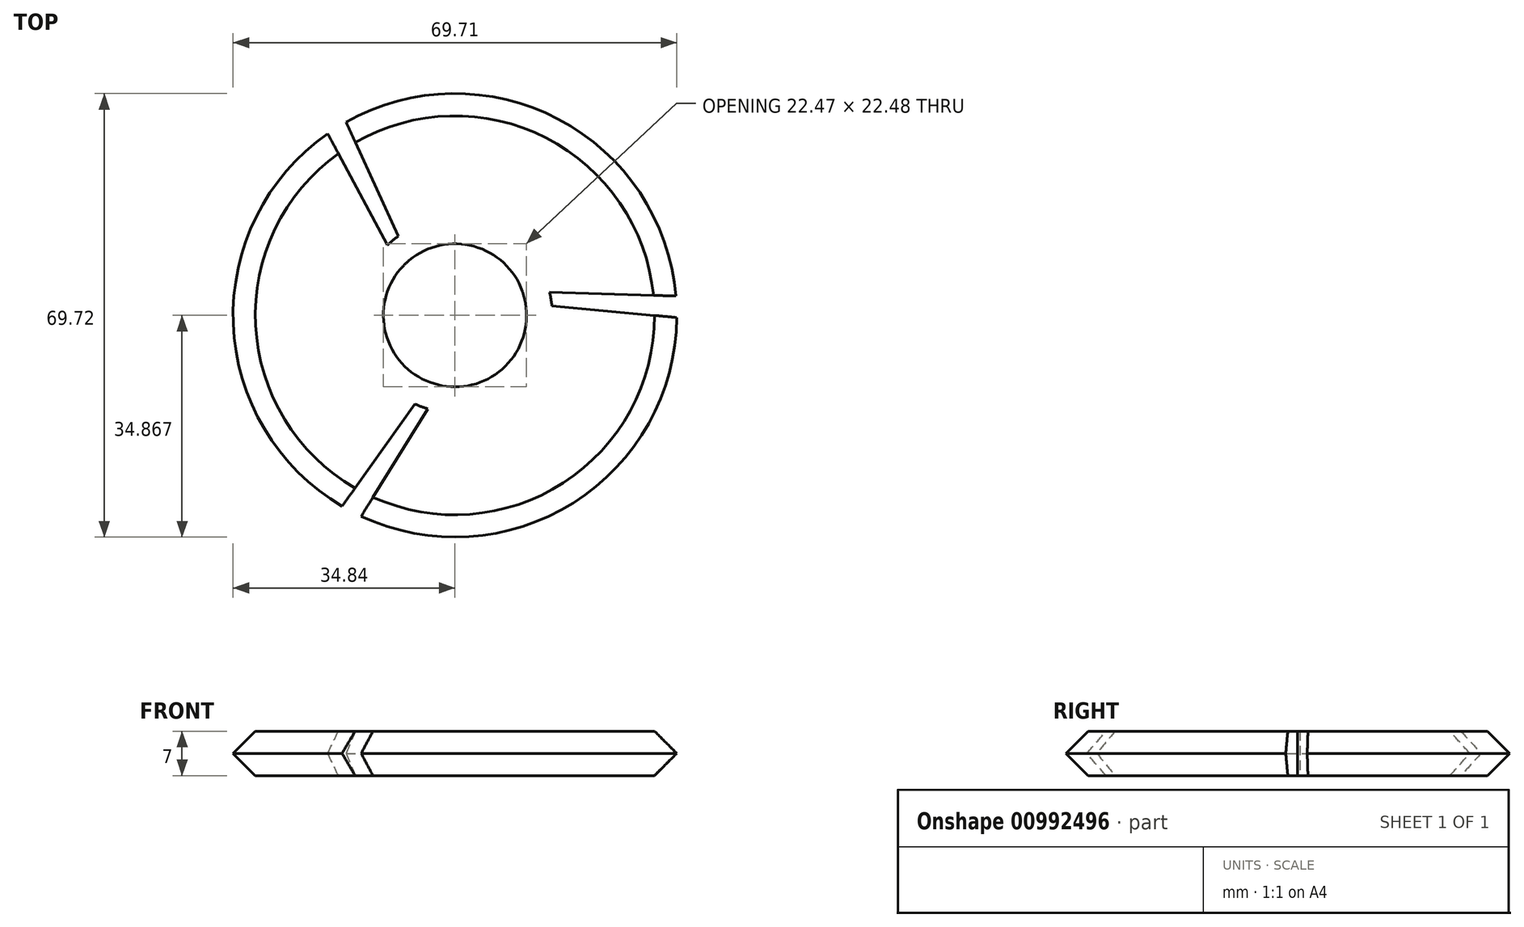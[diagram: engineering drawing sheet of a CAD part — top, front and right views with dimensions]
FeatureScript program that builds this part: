
annotation { "Feature Type Name" : "Feature", "Feature Type Description" : "" }
export const myFeature = defineFeature(function(context is Context, id is Id, definition is map)
    precondition{}
    {
        {
            var Q0;
            Q0=qCreatedBy(makeId("Top.planeOp"),FACE);
            var sketch = newSketch(context, id + "F0", { "sketchPlane" : qUnion([Q0])});
            skArc(sketch, "E0", {"start": v(-12.4, -17.28) * mm, "mid": v(-2.48, -14.21) * mm, "end": v(0.7, -4.33) * mm});
            skCircle(sketch, "E1", {"center": v(-10.39, -6.21) * mm, "radius": 35.36 * mm});
            skLineSegment(sketch, "E2", {"start": v(-14.3, -16.76) * mm, "end": v(-28.4, -36.63) * mm});
            skLineSegment(sketch, "E3", {"start": v(-28.4, -36.63) * mm, "end": v(-25.39, -38.23) * mm});
            skLineSegment(sketch, "E4", {"start": v(-25.39, -38.23) * mm, "end": v(-12.4, -17.28) * mm});
            skLineSegment(sketch, "E5", {"start": v(-12.4, -17.28) * mm, "end": v(-14.3, -16.76) * mm});
            skLineSegment(sketch, "E6.1.0", {"start": v(24.84, -3.2) * mm, "end": v(0.2, -2.42) * mm});
            skLineSegment(sketch, "E6.1.1", {"start": v(0.7, -4.33) * mm, "end": v(24.97, -6.6) * mm});
            skLineSegment(sketch, "E6.2.0", {"start": v(-30.61, 22.8) * mm, "end": v(-18.96, 1.07) * mm});
            skLineSegment(sketch, "E6.2.1", {"start": v(-17.56, 2.45) * mm, "end": v(-27.72, 24.6) * mm});
            skCircle(sketch, "E7", {"center": v(-10.39, -6.21) * mm, "radius": 15.3 * mm});
            skCircle(sketch, "E8", {"center": v(-10.39, -6.21) * mm, "radius": 40.8 * mm});
            skArc(sketch, "E9.trimOffspring", {"start": v(-18.96, 1.07) * mm, "mid": v(-21.27, -9.06) * mm, "end": v(-14.3, -16.76) * mm});
            skArc(sketch, "E10.trimOffspring", {"start": v(0.2, -2.42) * mm, "mid": v(-7.4, 4.64) * mm, "end": v(-17.56, 2.45) * mm});
            skArc(sketch, "E11", {"start": v(0.7, -4.33) * mm, "mid": v(0.48, -3.37) * mm, "end": v(0.2, -2.42) * mm});
            skArc(sketch, "E12", {"start": v(-17.56, 2.45) * mm, "mid": v(-18.28, 1.78) * mm, "end": v(-18.96, 1.07) * mm});
            skSolve(sketch);
        }
        {
            var Q0;
            {var subQ1=sQuery(id+"F0.wireOp",EDGE,"E1");var subQ3=sQuery(id+"F0.wireOp",EDGE,"E6.2.0");var subQ4=makeQuery(id+"F0.imprint","INTERSECT",VERTEX,{"derivedFrom":[subQ1,subQ3]});Q0=makeQuery(id+"F0.imprint","IMPRINT",FACE,{"disambiguationData":[TD([[makeQuery(id+"F0.imprint","IMPRINT",EDGE,{"disambiguationData":[TD([[subQ4,-1.0]])],"derivedFrom":subQ3}),-1.0]])]});}
            var Q1;
            {var subQ0=sQuery(id+"F0.wireOp",EDGE,"E6.1.0");var subQ1=sQuery(id+"F0.wireOp",EDGE,"E1");var subQ2=makeQuery(id+"F0.imprint","INTERSECT",VERTEX,{"derivedFrom":[subQ1,subQ0]});Q1=makeQuery(id+"F0.imprint","IMPRINT",FACE,{"disambiguationData":[TD([[makeQuery(id+"F0.imprint","IMPRINT",EDGE,{"disambiguationData":[TD([[subQ2,-1.0]])],"derivedFrom":subQ1}),1.0]])]});}
            var Q2;
            {var subQ1=sQuery(id+"F0.wireOp",EDGE,"E1");var subQ3=sQuery(id+"F0.wireOp",EDGE,"E6.1.1");var subQ4=makeQuery(id+"F0.imprint","INTERSECT",VERTEX,{"derivedFrom":[subQ1,subQ3]});Q2=makeQuery(id+"F0.imprint","IMPRINT",FACE,{"disambiguationData":[TD([[makeQuery(id+"F0.imprint","IMPRINT",EDGE,{"disambiguationData":[TD([[subQ4,1.0]])],"derivedFrom":subQ3}),-1.0]])]});}
            var Q3;
            {var subQ0=sQuery(id+"F0.wireOp",EDGE,"E9.trimOffspring");Q3=makeQuery(id+"F0.imprint","IMPRINT",FACE,{"disambiguationData":[TD([[makeQuery(id+"F0.imprint","IMPRINT",EDGE,{"derivedFrom":subQ0}),-1.0]])]});}
            var Q4;
            {var subQ0=sQuery(id+"F0.wireOp",EDGE,"E10.trimOffspring");Q4=makeQuery(id+"F0.imprint","IMPRINT",FACE,{"disambiguationData":[TD([[makeQuery(id+"F0.imprint","IMPRINT",EDGE,{"derivedFrom":subQ0}),-1.0]])]});}
            var Q5;
            {var subQ0=sQuery(id+"F0.wireOp",EDGE,"E0");Q5=makeQuery(id+"F0.imprint","IMPRINT",FACE,{"disambiguationData":[TD([[makeQuery(id+"F0.imprint","IMPRINT",EDGE,{"derivedFrom":subQ0}),-1.0]])]});}
            var Q6;
            {var subQ0=sQuery(id+"F0.wireOp",EDGE,"E12");Q6=makeQuery(id+"F0.imprint","IMPRINT",FACE,{"disambiguationData":[TD([[makeQuery(id+"F0.imprint","IMPRINT",EDGE,{"derivedFrom":subQ0}),-1.0]])]});}
            var Q7;
            {var subQ0=sQuery(id+"F0.wireOp",EDGE,"E11");Q7=makeQuery(id+"F0.imprint","IMPRINT",FACE,{"disambiguationData":[TD([[makeQuery(id+"F0.imprint","IMPRINT",EDGE,{"derivedFrom":subQ0}),-1.0]])]});}
            var Q8;
            {var subQ0=sQuery(id+"F0.wireOp",EDGE,"E5");Q8=makeQuery(id+"F0.imprint","IMPRINT",FACE,{"disambiguationData":[TD([[makeQuery(id+"F0.imprint","IMPRINT",EDGE,{"derivedFrom":subQ0}),1.0]])]});}
            extrude(context, id + "F1", {"entities" : qUnion([Q0, Q1, Q2, Q3, Q4, Q5, Q6, Q7, Q8]), "depth" : 7 * mm, "offsetDistance" : 25 * mm});
        }
        {
            var Q0;
            {var subQ0=sQuery(id+"F0.wireOp",EDGE,"E1");Q0=makeQuery(id+"F1.opExtrude","CAP_EDGE",EDGE,{"disambiguationData":[OSD([subQ0]),TDD([makeQuery(id+"F0.imprint","IMPRINT",EDGE,{"disambiguationData":[TD([[makeQuery(id+"F0.imprint","INTERSECT",VERTEX,{"derivedFrom":[subQ0,sQuery(id+"F0.wireOp",EDGE,"E6.2.0")]}),-1.0]])],"derivedFrom":subQ0})])],"isStart":false});}
            var Q1;
            {var subQ0=sQuery(id+"F0.wireOp",EDGE,"E1");Q1=makeQuery(id+"F1.opExtrude","CAP_EDGE",EDGE,{"disambiguationData":[OSD([subQ0]),TDD([makeQuery(id+"F0.imprint","IMPRINT",EDGE,{"disambiguationData":[TD([[makeQuery(id+"F0.imprint","INTERSECT",VERTEX,{"derivedFrom":[subQ0,sQuery(id+"F0.wireOp",EDGE,"E6.2.0")]}),-1.0]])],"derivedFrom":subQ0})])],"isStart":true});}
            var Q2;
            {var subQ0=sQuery(id+"F0.wireOp",EDGE,"E1");Q2=makeQuery(id+"F1.opExtrude","CAP_EDGE",EDGE,{"disambiguationData":[OSD([subQ0]),TDD([makeQuery(id+"F0.imprint","IMPRINT",EDGE,{"disambiguationData":[TD([[makeQuery(id+"F0.imprint","INTERSECT",VERTEX,{"derivedFrom":[subQ0,sQuery(id+"F0.wireOp",EDGE,"E6.1.1")]}),1.0]])],"derivedFrom":subQ0})])],"isStart":false});}
            var Q3;
            {var subQ0=sQuery(id+"F0.wireOp",EDGE,"E1");Q3=makeQuery(id+"F1.opExtrude","CAP_EDGE",EDGE,{"disambiguationData":[OSD([subQ0]),TDD([makeQuery(id+"F0.imprint","IMPRINT",EDGE,{"disambiguationData":[TD([[makeQuery(id+"F0.imprint","INTERSECT",VERTEX,{"derivedFrom":[subQ0,sQuery(id+"F0.wireOp",EDGE,"E6.1.1")]}),1.0]])],"derivedFrom":subQ0})])],"isStart":true});}
            var Q4;
            {var subQ0=sQuery(id+"F0.wireOp",EDGE,"E1");Q4=makeQuery(id+"F1.opExtrude","CAP_EDGE",EDGE,{"disambiguationData":[OSD([subQ0]),TDD([makeQuery(id+"F0.imprint","IMPRINT",EDGE,{"disambiguationData":[TD([[makeQuery(id+"F0.imprint","INTERSECT",VERTEX,{"derivedFrom":[subQ0,sQuery(id+"F0.wireOp",EDGE,"E6.1.0")]}),-1.0]])],"derivedFrom":subQ0})])],"isStart":false});}
            var Q5;
            {var subQ0=sQuery(id+"F0.wireOp",EDGE,"E1");Q5=makeQuery(id+"F1.opExtrude","CAP_EDGE",EDGE,{"disambiguationData":[OSD([subQ0]),TDD([makeQuery(id+"F0.imprint","IMPRINT",EDGE,{"disambiguationData":[TD([[makeQuery(id+"F0.imprint","INTERSECT",VERTEX,{"derivedFrom":[subQ0,sQuery(id+"F0.wireOp",EDGE,"E6.1.0")]}),-1.0]])],"derivedFrom":subQ0})])],"isStart":true});}
            chamfer(context, id + "F2", {"entities" : qUnion([Q0, Q1, Q2, Q3, Q4, Q5]), "width" : 4 * mm, "tangentPropagation" : true});
        }
    });
